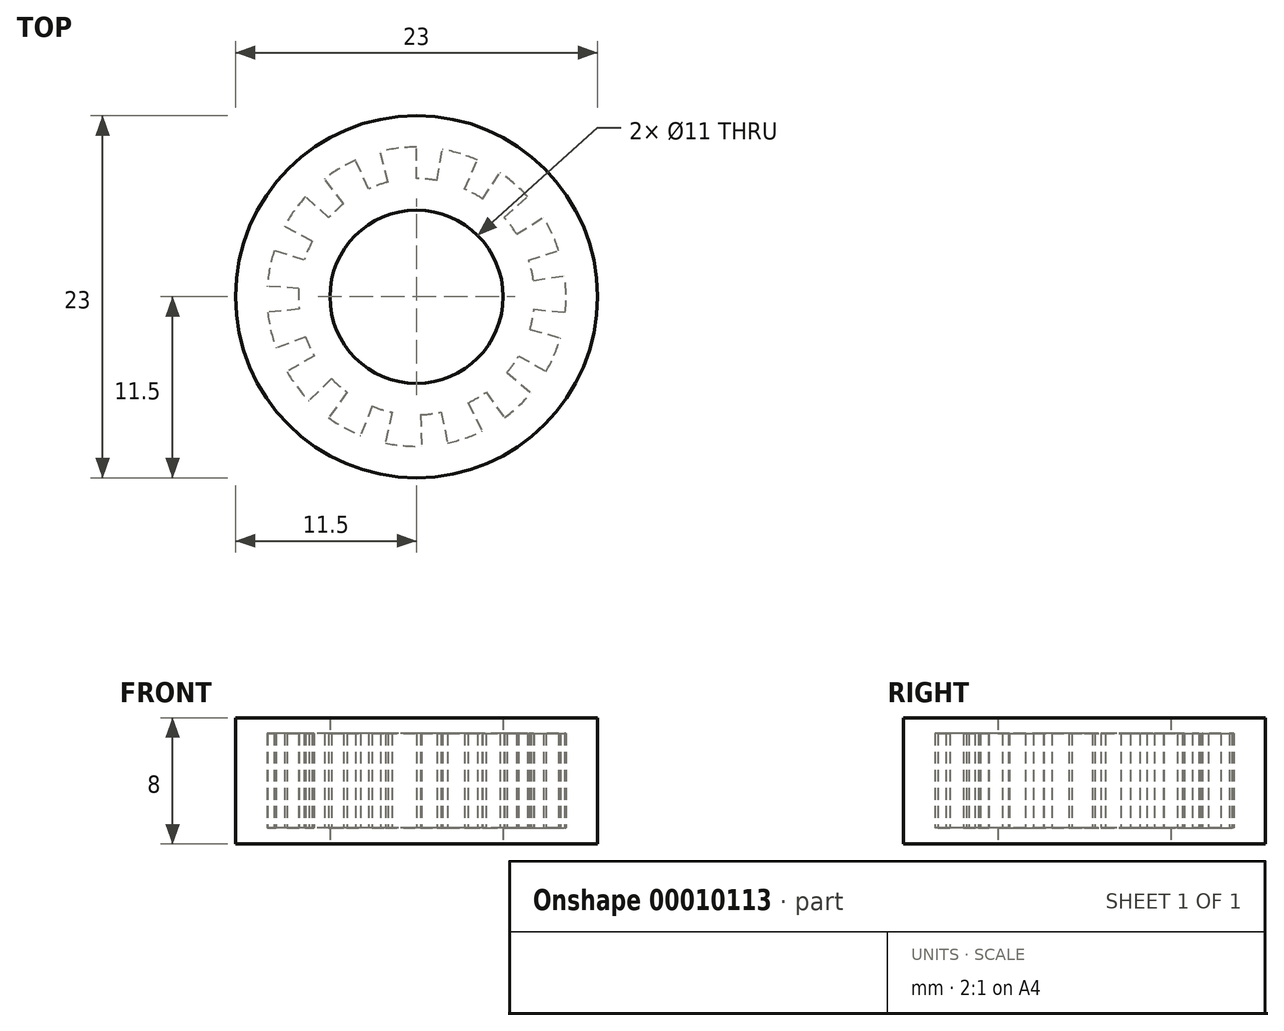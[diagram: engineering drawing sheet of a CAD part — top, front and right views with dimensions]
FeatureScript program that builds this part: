
annotation { "Feature Type Name" : "Feature", "Feature Type Description" : "" }
export const myFeature = defineFeature(function(context is Context, id is Id, definition is map)
    precondition{}
    {
        {
            var Q0;
            Q0=qCreatedBy(makeId("Top.planeOp"),FACE);
            var sketch = newSketch(context, id + "F0", { "sketchPlane" : qUnion([Q0])});
            skCircle(sketch, "E0", {"center": v(0, 0) * mm, "radius": 11.5 * mm});
            skCircle(sketch, "E1", {"center": v(0, 0) * mm, "radius": 5.5 * mm});
            skSolve(sketch);
        }
        {
            var Q0;
            Q0=makeQuery(id+"F0.imprint","IMPRINT",FACE,{"disambiguationData":[TD([[makeQuery(id+"F0.imprint","IMPRINT",EDGE,{"derivedFrom":sQuery(id+"F0.wireOp",EDGE,"E0")}),1.0]])]});
            extrude(context, id + "F1", {"entities" : qUnion([Q0]), "depth" : 1 * mm});
        }
        {
            var Q0;
            Q0=makeQuery(id+"F1.opExtrude","CAP_FACE",FACE,{"disambiguationData":[OSD([sQuery(id+"F0.wireOp",EDGE,"E0"),sQuery(id+"F0.wireOp",EDGE,"E1")])],"isStart":false});
            var sketch = newSketch(context, id + "F2", { "sketchPlane" : qUnion([Q0])});
            skCircle(sketch, "E2", {"center": v(0, 0) * mm, "radius": 11.5 * mm});
            skLineSegment(sketch, "E3", {"start": v(0, 0) * mm, "end": v(0, 7.5) * mm, "construction": true});
            skLineSegment(sketch, "E4", {"start": v(0, 7.5) * mm, "end": v(0, 9.5) * mm});
            skLineSegment(sketch, "E5", {"start": v(0, 0) * mm, "end": v(-1.81, 7.28) * mm, "construction": true});
            skLineSegment(sketch, "E6", {"start": v(-1.81, 7.28) * mm, "end": v(-2.3, 9.22) * mm});
            skLineSegment(sketch, "E7", {"start": v(0, 0) * mm, "end": v(-3.05, 6.85) * mm, "construction": true});
            skArc(sketch, "E8", {"start": v(0, 9.5) * mm, "mid": v(-1.16, 9.43) * mm, "end": v(-2.3, 9.22) * mm});
            skArc(sketch, "E9", {"start": v(-1.81, 7.28) * mm, "mid": v(-2.44, 7.1) * mm, "end": v(-3.05, 6.85) * mm});
            skArc(sketch, "E10.1.0", {"start": v(-4.62, 5.91) * mm, "mid": v(-5.11, 5.49) * mm, "end": v(-5.57, 5.02) * mm});
            skLineSegment(sketch, "E10.1.1", {"start": v(-4.62, 5.91) * mm, "end": v(-5.85, 7.49) * mm});
            skArc(sketch, "E10.1.2", {"start": v(-3.86, 8.68) * mm, "mid": v(-4.9, 8.14) * mm, "end": v(-5.85, 7.49) * mm});
            skLineSegment(sketch, "E10.1.3", {"start": v(-3.05, 6.85) * mm, "end": v(-3.86, 8.68) * mm});
            skArc(sketch, "E10.2.0", {"start": v(-6.62, 3.52) * mm, "mid": v(-6.9, 2.93) * mm, "end": v(-7.13, 2.32) * mm});
            skLineSegment(sketch, "E10.2.1", {"start": v(-6.62, 3.52) * mm, "end": v(-8.39, 4.46) * mm});
            skArc(sketch, "E10.2.2", {"start": v(-7.06, 6.36) * mm, "mid": v(-7.78, 5.45) * mm, "end": v(-8.39, 4.46) * mm});
            skLineSegment(sketch, "E10.2.3", {"start": v(-5.57, 5.02) * mm, "end": v(-7.06, 6.36) * mm});
            skArc(sketch, "E10.3.0", {"start": v(-7.48, 0.52) * mm, "mid": v(-7.5, -0.13) * mm, "end": v(-7.46, -0.78) * mm});
            skLineSegment(sketch, "E10.3.1", {"start": v(-7.48, 0.52) * mm, "end": v(-9.48, 0.66) * mm});
            skArc(sketch, "E10.3.2", {"start": v(-9.04, 2.94) * mm, "mid": v(-9.33, 1.81) * mm, "end": v(-9.48, 0.66) * mm});
            skLineSegment(sketch, "E10.3.3", {"start": v(-7.13, 2.32) * mm, "end": v(-9.04, 2.94) * mm});
            skArc(sketch, "E10.4.0", {"start": v(-7.05, -2.57) * mm, "mid": v(-6.8, -3.17) * mm, "end": v(-6.5, -3.75) * mm});
            skLineSegment(sketch, "E10.4.1", {"start": v(-7.05, -2.57) * mm, "end": v(-8.93, -3.25) * mm});
            skArc(sketch, "E10.4.2", {"start": v(-9.45, -1) * mm, "mid": v(-9.26, -2.14) * mm, "end": v(-8.93, -3.25) * mm});
            skLineSegment(sketch, "E10.4.3", {"start": v(-7.46, -0.78) * mm, "end": v(-9.45, -1) * mm});
            skArc(sketch, "E10.5.0", {"start": v(-5.4, -5.2) * mm, "mid": v(-4.92, -5.66) * mm, "end": v(-4.4, -6.07) * mm});
            skLineSegment(sketch, "E10.5.1", {"start": v(-5.4, -5.2) * mm, "end": v(-6.83, -6.6) * mm});
            skArc(sketch, "E10.5.2", {"start": v(-8.23, -4.75) * mm, "mid": v(-7.59, -5.72) * mm, "end": v(-6.83, -6.6) * mm});
            skLineSegment(sketch, "E10.5.3", {"start": v(-6.5, -3.75) * mm, "end": v(-8.23, -4.75) * mm});
            skArc(sketch, "E10.6.0", {"start": v(-2.8, -6.95) * mm, "mid": v(-2.2, -7.17) * mm, "end": v(-1.56, -7.34) * mm});
            skLineSegment(sketch, "E10.6.1", {"start": v(-2.8, -6.95) * mm, "end": v(-3.56, -8.8) * mm});
            skArc(sketch, "E10.6.2", {"start": v(-5.58, -7.69) * mm, "mid": v(-4.6, -8.3) * mm, "end": v(-3.56, -8.8) * mm});
            skLineSegment(sketch, "E10.6.3", {"start": v(-4.4, -6.07) * mm, "end": v(-5.58, -7.69) * mm});
            skArc(sketch, "E10.7.0", {"start": v(0.26, -7.5) * mm, "mid": v(0.91, -7.44) * mm, "end": v(1.56, -7.34) * mm});
            skLineSegment(sketch, "E10.7.1", {"start": v(0.26, -7.5) * mm, "end": v(0.33, -9.5) * mm});
            skArc(sketch, "E10.7.2", {"start": v(-1.98, -9.3) * mm, "mid": v(-0.83, -9.46) * mm, "end": v(0.33, -9.5) * mm});
            skLineSegment(sketch, "E10.7.3", {"start": v(-1.56, -7.34) * mm, "end": v(-1.98, -9.3) * mm});
            skArc(sketch, "E10.8.0", {"start": v(3.29, -6.74) * mm, "mid": v(3.86, -6.43) * mm, "end": v(4.4, -6.07) * mm});
            skLineSegment(sketch, "E10.8.1", {"start": v(3.29, -6.74) * mm, "end": v(4.16, -8.54) * mm});
            skArc(sketch, "E10.8.2", {"start": v(1.98, -9.3) * mm, "mid": v(3.1, -8.98) * mm, "end": v(4.16, -8.54) * mm});
            skLineSegment(sketch, "E10.8.3", {"start": v(1.56, -7.34) * mm, "end": v(1.98, -9.3) * mm});
            skArc(sketch, "E10.9.0", {"start": v(5.75, -4.82) * mm, "mid": v(6.14, -4.3) * mm, "end": v(6.5, -3.75) * mm});
            skLineSegment(sketch, "E10.9.1", {"start": v(5.75, -4.82) * mm, "end": v(7.28, -6.1) * mm});
            skArc(sketch, "E10.9.2", {"start": v(5.58, -7.69) * mm, "mid": v(6.48, -6.95) * mm, "end": v(7.28, -6.1) * mm});
            skLineSegment(sketch, "E10.9.3", {"start": v(4.4, -6.07) * mm, "end": v(5.58, -7.69) * mm});
            skArc(sketch, "E10.10.0", {"start": v(7.2, -2.07) * mm, "mid": v(7.36, -1.43) * mm, "end": v(7.46, -0.78) * mm});
            skLineSegment(sketch, "E10.10.1", {"start": v(7.2, -2.07) * mm, "end": v(9.13, -2.62) * mm});
            skArc(sketch, "E10.10.2", {"start": v(8.23, -4.75) * mm, "mid": v(8.74, -3.71) * mm, "end": v(9.13, -2.62) * mm});
            skLineSegment(sketch, "E10.10.3", {"start": v(6.5, -3.75) * mm, "end": v(8.23, -4.75) * mm});
            skArc(sketch, "E10.11.0", {"start": v(7.43, 1.04) * mm, "mid": v(7.3, 1.69) * mm, "end": v(7.13, 2.32) * mm});
            skLineSegment(sketch, "E10.11.1", {"start": v(7.43, 1.04) * mm, "end": v(9.4, 1.32) * mm});
            skArc(sketch, "E10.11.2", {"start": v(9.45, -1) * mm, "mid": v(9.5, 0.17) * mm, "end": v(9.4, 1.32) * mm});
            skLineSegment(sketch, "E10.11.3", {"start": v(7.46, -0.78) * mm, "end": v(9.45, -1) * mm});
            skArc(sketch, "E10.12.0", {"start": v(6.36, 3.97) * mm, "mid": v(5.99, 4.51) * mm, "end": v(5.57, 5.02) * mm});
            skLineSegment(sketch, "E10.12.1", {"start": v(6.36, 3.97) * mm, "end": v(8.06, 5.03) * mm});
            skArc(sketch, "E10.12.2", {"start": v(9.04, 2.94) * mm, "mid": v(8.6, 4.01) * mm, "end": v(8.06, 5.03) * mm});
            skLineSegment(sketch, "E10.12.3", {"start": v(7.13, 2.32) * mm, "end": v(9.04, 2.94) * mm});
            skArc(sketch, "E10.13.0", {"start": v(4.2, 6.22) * mm, "mid": v(3.64, 6.56) * mm, "end": v(3.05, 6.85) * mm});
            skLineSegment(sketch, "E10.13.1", {"start": v(4.2, 6.22) * mm, "end": v(5.31, 7.88) * mm});
            skArc(sketch, "E10.13.2", {"start": v(7.06, 6.36) * mm, "mid": v(6.23, 7.17) * mm, "end": v(5.31, 7.88) * mm});
            skLineSegment(sketch, "E10.13.3", {"start": v(5.57, 5.02) * mm, "end": v(7.06, 6.36) * mm});
            skArc(sketch, "E10.14.0", {"start": v(1.3, 7.39) * mm, "mid": v(0.65, 7.47) * mm, "end": v(0, 7.5) * mm});
            skLineSegment(sketch, "E10.14.1", {"start": v(1.3, 7.39) * mm, "end": v(1.65, 9.36) * mm});
            skArc(sketch, "E10.14.2", {"start": v(3.86, 8.68) * mm, "mid": v(2.78, 9.08) * mm, "end": v(1.65, 9.36) * mm});
            skLineSegment(sketch, "E10.14.3", {"start": v(3.05, 6.85) * mm, "end": v(3.86, 8.68) * mm});
            skSolve(sketch);
        }
        {
            var Q0;
            Q0=makeQuery(id+"F2.imprint","IMPRINT",FACE,{"disambiguationData":[TD([[makeQuery(id+"F2.imprint","IMPRINT",EDGE,{"derivedFrom":sQuery(id+"F2.wireOp",EDGE,"E2")}),1.0]])]});
            extrude(context, id + "F3", {"entities" : qUnion([Q0]), "operationType" : NewBodyOperationType.ADD, "depth" : 6 * mm});
        }
        {
            var Q0;
            Q0=makeQuery(id+"F3.opExtrude","CAP_FACE",FACE,{"disambiguationData":[OSD([sQuery(id+"F2.wireOp",EDGE,"E2"),sQuery(id+"F2.wireOp",EDGE,"E4"),sQuery(id+"F2.wireOp",EDGE,"E6"),sQuery(id+"F2.wireOp",EDGE,"E8"),sQuery(id+"F2.wireOp",EDGE,"E9"),sQuery(id+"F2.wireOp",EDGE,"E10.1.0"),sQuery(id+"F2.wireOp",EDGE,"E10.1.1"),sQuery(id+"F2.wireOp",EDGE,"E10.1.2"),sQuery(id+"F2.wireOp",EDGE,"E10.1.3"),sQuery(id+"F2.wireOp",EDGE,"E10.2.0"),sQuery(id+"F2.wireOp",EDGE,"E10.2.1"),sQuery(id+"F2.wireOp",EDGE,"E10.2.2"),sQuery(id+"F2.wireOp",EDGE,"E10.2.3"),sQuery(id+"F2.wireOp",EDGE,"E10.3.0"),sQuery(id+"F2.wireOp",EDGE,"E10.3.1"),sQuery(id+"F2.wireOp",EDGE,"E10.3.2"),sQuery(id+"F2.wireOp",EDGE,"E10.3.3"),sQuery(id+"F2.wireOp",EDGE,"E10.4.0"),sQuery(id+"F2.wireOp",EDGE,"E10.4.1"),sQuery(id+"F2.wireOp",EDGE,"E10.4.2"),sQuery(id+"F2.wireOp",EDGE,"E10.4.3"),sQuery(id+"F2.wireOp",EDGE,"E10.5.0"),sQuery(id+"F2.wireOp",EDGE,"E10.5.1"),sQuery(id+"F2.wireOp",EDGE,"E10.5.2"),sQuery(id+"F2.wireOp",EDGE,"E10.5.3"),sQuery(id+"F2.wireOp",EDGE,"E10.6.0"),sQuery(id+"F2.wireOp",EDGE,"E10.6.1"),sQuery(id+"F2.wireOp",EDGE,"E10.6.2"),sQuery(id+"F2.wireOp",EDGE,"E10.6.3"),sQuery(id+"F2.wireOp",EDGE,"E10.7.0"),sQuery(id+"F2.wireOp",EDGE,"E10.7.1"),sQuery(id+"F2.wireOp",EDGE,"E10.7.2"),sQuery(id+"F2.wireOp",EDGE,"E10.7.3"),sQuery(id+"F2.wireOp",EDGE,"E10.8.0"),sQuery(id+"F2.wireOp",EDGE,"E10.8.1"),sQuery(id+"F2.wireOp",EDGE,"E10.8.2"),sQuery(id+"F2.wireOp",EDGE,"E10.8.3"),sQuery(id+"F2.wireOp",EDGE,"E10.9.0"),sQuery(id+"F2.wireOp",EDGE,"E10.9.1"),sQuery(id+"F2.wireOp",EDGE,"E10.9.2"),sQuery(id+"F2.wireOp",EDGE,"E10.9.3"),sQuery(id+"F2.wireOp",EDGE,"E10.10.0"),sQuery(id+"F2.wireOp",EDGE,"E10.10.1"),sQuery(id+"F2.wireOp",EDGE,"E10.10.2"),sQuery(id+"F2.wireOp",EDGE,"E10.10.3"),sQuery(id+"F2.wireOp",EDGE,"E10.11.0"),sQuery(id+"F2.wireOp",EDGE,"E10.11.1"),sQuery(id+"F2.wireOp",EDGE,"E10.11.2"),sQuery(id+"F2.wireOp",EDGE,"E10.11.3"),sQuery(id+"F2.wireOp",EDGE,"E10.12.0"),sQuery(id+"F2.wireOp",EDGE,"E10.12.1"),sQuery(id+"F2.wireOp",EDGE,"E10.12.2"),sQuery(id+"F2.wireOp",EDGE,"E10.12.3"),sQuery(id+"F2.wireOp",EDGE,"E10.13.0"),sQuery(id+"F2.wireOp",EDGE,"E10.13.1"),sQuery(id+"F2.wireOp",EDGE,"E10.13.2"),sQuery(id+"F2.wireOp",EDGE,"E10.13.3"),sQuery(id+"F2.wireOp",EDGE,"E10.14.0"),sQuery(id+"F2.wireOp",EDGE,"E10.14.1"),sQuery(id+"F2.wireOp",EDGE,"E10.14.2"),sQuery(id+"F2.wireOp",EDGE,"E10.14.3")])],"isStart":false});
            var sketch = newSketch(context, id + "F4", { "sketchPlane" : qUnion([Q0])});
            skCircle(sketch, "E11", {"center": v(0, 0) * mm, "radius": 5.5 * mm});
            skCircle(sketch, "E12", {"center": v(0, 0) * mm, "radius": 11.5 * mm});
            skSolve(sketch);
        }
        {
            var Q0;
            Q0 = qSketchRegion(id + "F4", true);
            extrude(context, id + "F5", {"entities" : qUnion([Q0]), "operationType" : NewBodyOperationType.ADD, "depth" : 1 * mm});
        }
    });
